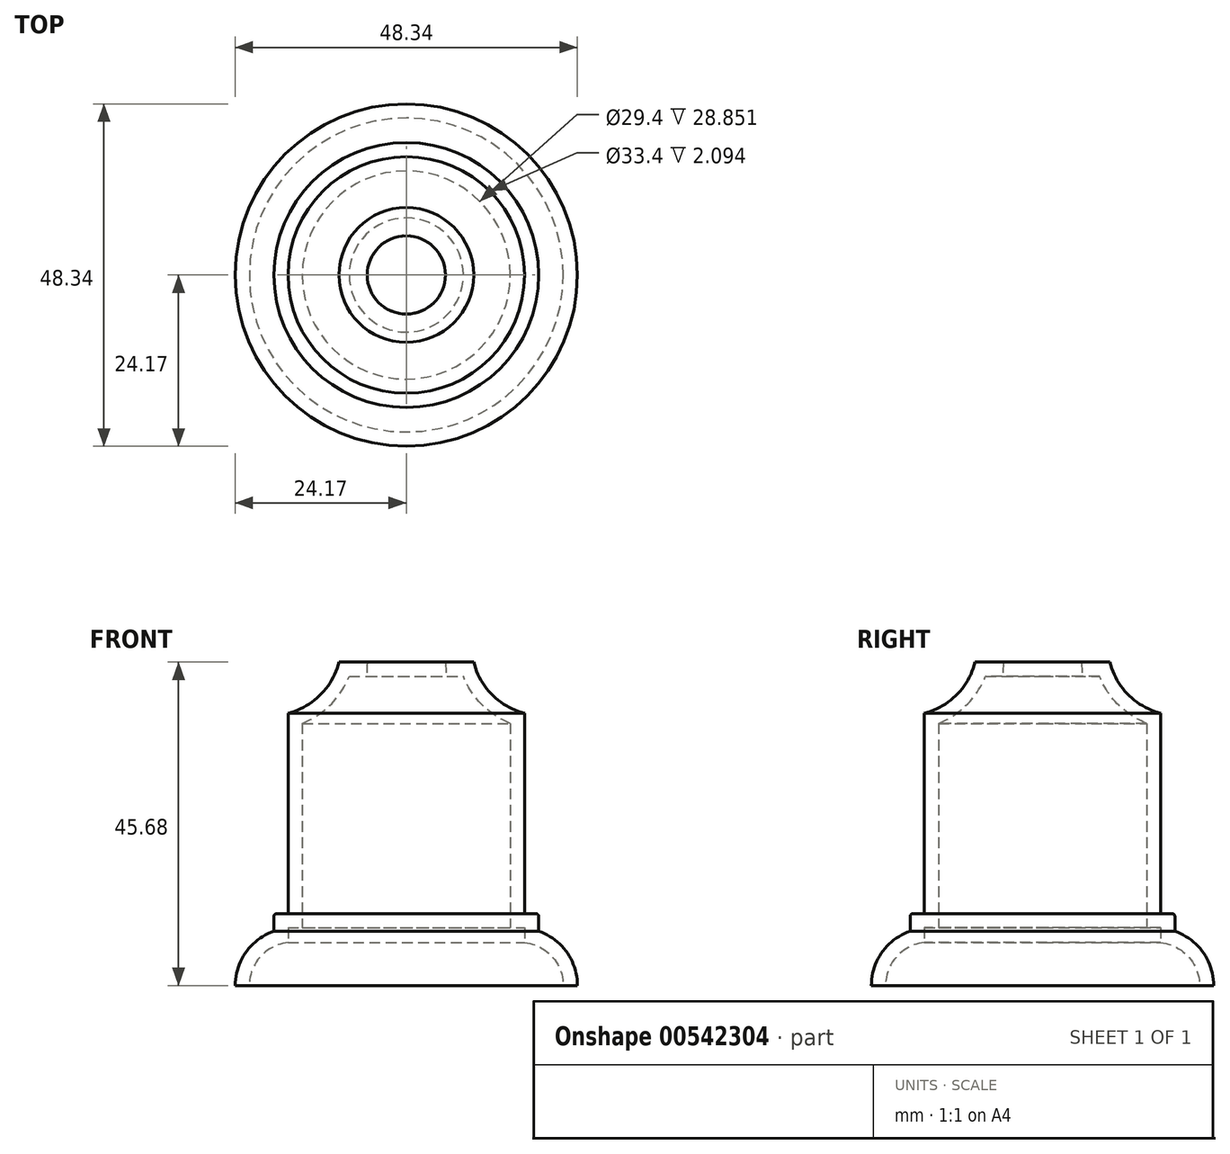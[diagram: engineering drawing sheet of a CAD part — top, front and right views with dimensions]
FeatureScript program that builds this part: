
annotation { "Feature Type Name" : "Feature", "Feature Type Description" : "" }
export const myFeature = defineFeature(function(context is Context, id is Id, definition is map)
    precondition{}
    {
        {
            var Q0;
            Q0=qCreatedBy(makeId("Front.planeOp"),FACE);
            var sketch = newSketch(context, id + "F0", { "sketchPlane" : qUnion([Q0])});
            skLineSegment(sketch, "E0", {"start": v(5.52, 47.25) * mm, "end": v(9.52, 47.25) * mm});
            skLineSegment(sketch, "E1", {"start": v(16.7, 40.03) * mm, "end": v(16.7, 11.73) * mm});
            skLineSegment(sketch, "E2", {"start": v(16.7, 11.73) * mm, "end": v(18.3, 11.73) * mm});
            skLineSegment(sketch, "E3", {"start": v(18.7, 11.33) * mm, "end": v(18.7, 9.23) * mm});
            skArc(sketch, "E4", {"start": v(24.17, 1.57) * mm, "mid": v(22.66, 6.28) * mm, "end": v(18.7, 9.23) * mm});
            skArc(sketch, "E5", {"start": v(9.52, 47.25) * mm, "mid": v(12.1, 42.64) * mm, "end": v(16.7, 40.03) * mm});
            skPoint(sketch, "E6.visualSharp", {"position": v(18.7, 11.73) * mm});
            skArc(sketch, "E6.filletArc", {"start": v(18.7, 11.33) * mm, "mid": v(18.58, 11.61) * mm, "end": v(18.3, 11.73) * mm});
            skArc(sketch, "E7.0", {"start": v(22.17, 1.57) * mm, "mid": v(20.6, 5.65) * mm, "end": v(16.7, 7.64) * mm});
            skLineSegment(sketch, "E7.1", {"start": v(16.7, 9.73) * mm, "end": v(16.7, 7.64) * mm});
            skLineSegment(sketch, "E7.2", {"start": v(5.61, 45.25) * mm, "end": v(8.06, 45.25) * mm});
            skArc(sketch, "E7.3", {"start": v(8.06, 45.25) * mm, "mid": v(10.7, 41.23) * mm, "end": v(14.7, 38.58) * mm});
            skLineSegment(sketch, "E7.4", {"start": v(14.7, 38.58) * mm, "end": v(14.7, 9.73) * mm});
            skLineSegment(sketch, "E7.5", {"start": v(14.7, 9.73) * mm, "end": v(16.7, 9.73) * mm});
            skLineSegment(sketch, "E8", {"start": v(5.61, 45.25) * mm, "end": v(5.52, 47.25) * mm});
            skLineSegment(sketch, "E9", {"start": v(22.17, 1.57) * mm, "end": v(24.17, 1.57) * mm});
            skLineSegment(sketch, "E10", {"start": v(0, 0) * mm, "end": v(0, 15.37) * mm});
            skSolve(sketch);
        }
        {
            var Q0;
            Q0 = qSketchRegion(id + "F0", true);
            var Q1;
            Q1=sQuery(id+"F0.wireOp",EDGE,"E10");
            revolve(context, id + "F1", {"entities" : qUnion([Q0]), "axis" : qUnion([Q1]), "revolveType" : RevolveType.FULL});
        }
    });
